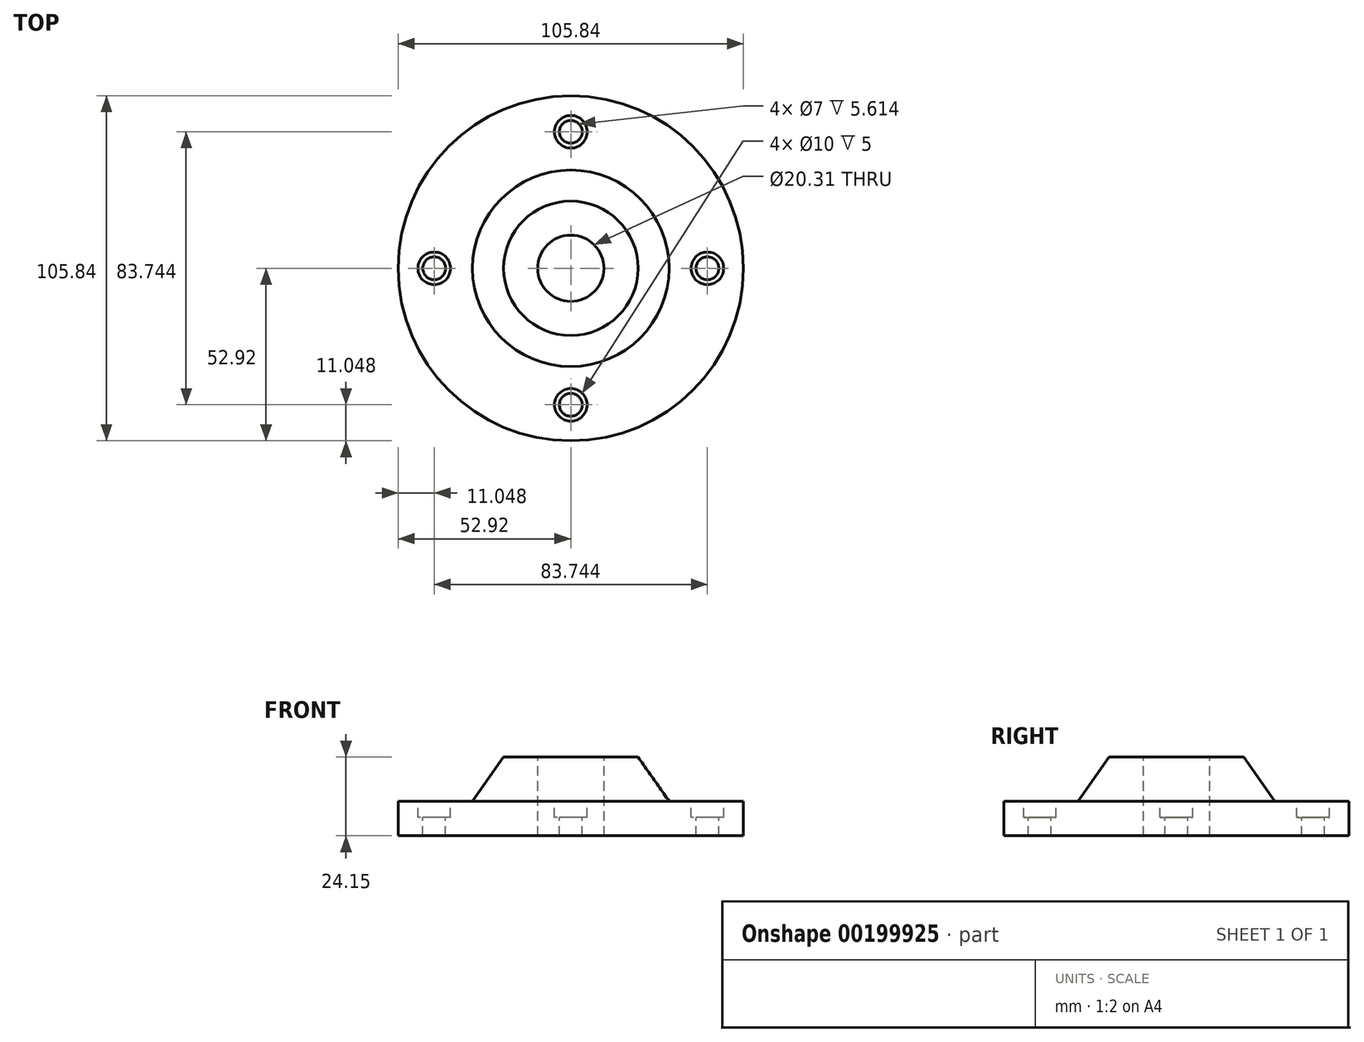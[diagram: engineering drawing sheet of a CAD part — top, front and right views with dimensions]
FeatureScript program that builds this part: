
annotation { "Feature Type Name" : "Feature", "Feature Type Description" : "" }
export const myFeature = defineFeature(function(context is Context, id is Id, definition is map)
    precondition{}
    {
        {
            var Q0;
            Q0=qCreatedBy(makeId("Front.planeOp"),FACE);
            var sketch = newSketch(context, id + "F0", { "sketchPlane" : qUnion([Q0])});
            skLineSegment(sketch, "E0", {"start": v(0, 53.69) * mm, "end": v(0, -43.84) * mm, "construction": true});
            skLineSegment(sketch, "E1", {"start": v(-10.15, 0) * mm, "end": v(-52.92, 0) * mm});
            skLineSegment(sketch, "E2", {"start": v(-52.92, 0) * mm, "end": v(-52.92, 10.61) * mm});
            skLineSegment(sketch, "E3", {"start": v(-52.92, 10.61) * mm, "end": v(-30.15, 10.61) * mm});
            skLineSegment(sketch, "E4", {"start": v(-30.15, 10.61) * mm, "end": v(-20.61, 24.15) * mm});
            skLineSegment(sketch, "E5", {"start": v(-20.61, 24.15) * mm, "end": v(-10.15, 24.15) * mm});
            skLineSegment(sketch, "E6", {"start": v(-10.15, 24.15) * mm, "end": v(-10.15, 0) * mm});
            skSolve(sketch);
        }
        {
            var Q0;
            Q0=makeQuery(id+"F0.imprint","IMPRINT",FACE,{"disambiguationData":[TD([[makeQuery(id+"F0.imprint","IMPRINT",EDGE,{"derivedFrom":sQuery(id+"F0.wireOp",EDGE,"E1")}),-1.0]])]});
            var Q1;
            Q1=sQuery(id+"F0.wireOp",EDGE,"E0");
            revolve(context, id + "F1", {"entities" : qUnion([Q0]), "axis" : qUnion([Q1]), "revolveType" : RevolveType.FULL});
        }
        {
            var Q0;
            Q0=makeQuery(id+"F1.opRevolve","SWEPT_FACE",FACE,{"disambiguationData":[OSD([sQuery(id+"F0.wireOp",EDGE,"E3")])]});
            var sketch = newSketch(context, id + "F2", { "sketchPlane" : qUnion([Q0])});
            skCircle(sketch, "E7", {"center": v(0, 0) * mm, "radius": 41.87 * mm});
            skCircle(sketch, "E8", {"center": v(0, 41.87) * mm, "radius": 5 * mm});
            skCircle(sketch, "E9", {"center": v(41.87, 0) * mm, "radius": 5 * mm});
            skCircle(sketch, "E10", {"center": v(-41.87, 0) * mm, "radius": 5 * mm});
            skCircle(sketch, "E11", {"center": v(0, -41.87) * mm, "radius": 5 * mm});
            skSolve(sketch);
        }
        {
            var Q0;
            Q0=sQuery(id+"F2.wireOp",VERTEX,"E10.center");
            var Q1;
            Q1=sQuery(id+"F2.wireOp",VERTEX,"E8.center");
            var Q2;
            Q2=sQuery(id+"F2.wireOp",VERTEX,"E9.center");
            var Q3;
            Q3=sQuery(id+"F2.wireOp",VERTEX,"E11.center");
            var Q4;
            Q4=makeQuery(id+"F1.opRevolve","SWEPT_BODY",BODY,{"disambiguationData":[OSD([sQuery(id+"F0.wireOp",EDGE,"E1"),sQuery(id+"F0.wireOp",EDGE,"E2"),sQuery(id+"F0.wireOp",EDGE,"E3"),sQuery(id+"F0.wireOp",EDGE,"E4"),sQuery(id+"F0.wireOp",EDGE,"E5"),sQuery(id+"F0.wireOp",EDGE,"E6")])]});
            hole(context, id + "F3", {"style" : HoleStyle.C_BORE, "endStyle" : HoleEndStyle.THROUGH, "holeDiameter" : 7 * mm, "cBoreDiameter" : 10 * mm, "cBoreDepth" : 5 * mm, "locations" : qUnion([Q0, Q1, Q2, Q3]), "scope" : qUnion([Q4]), "isTappedThrough" : true});
        }
    });
